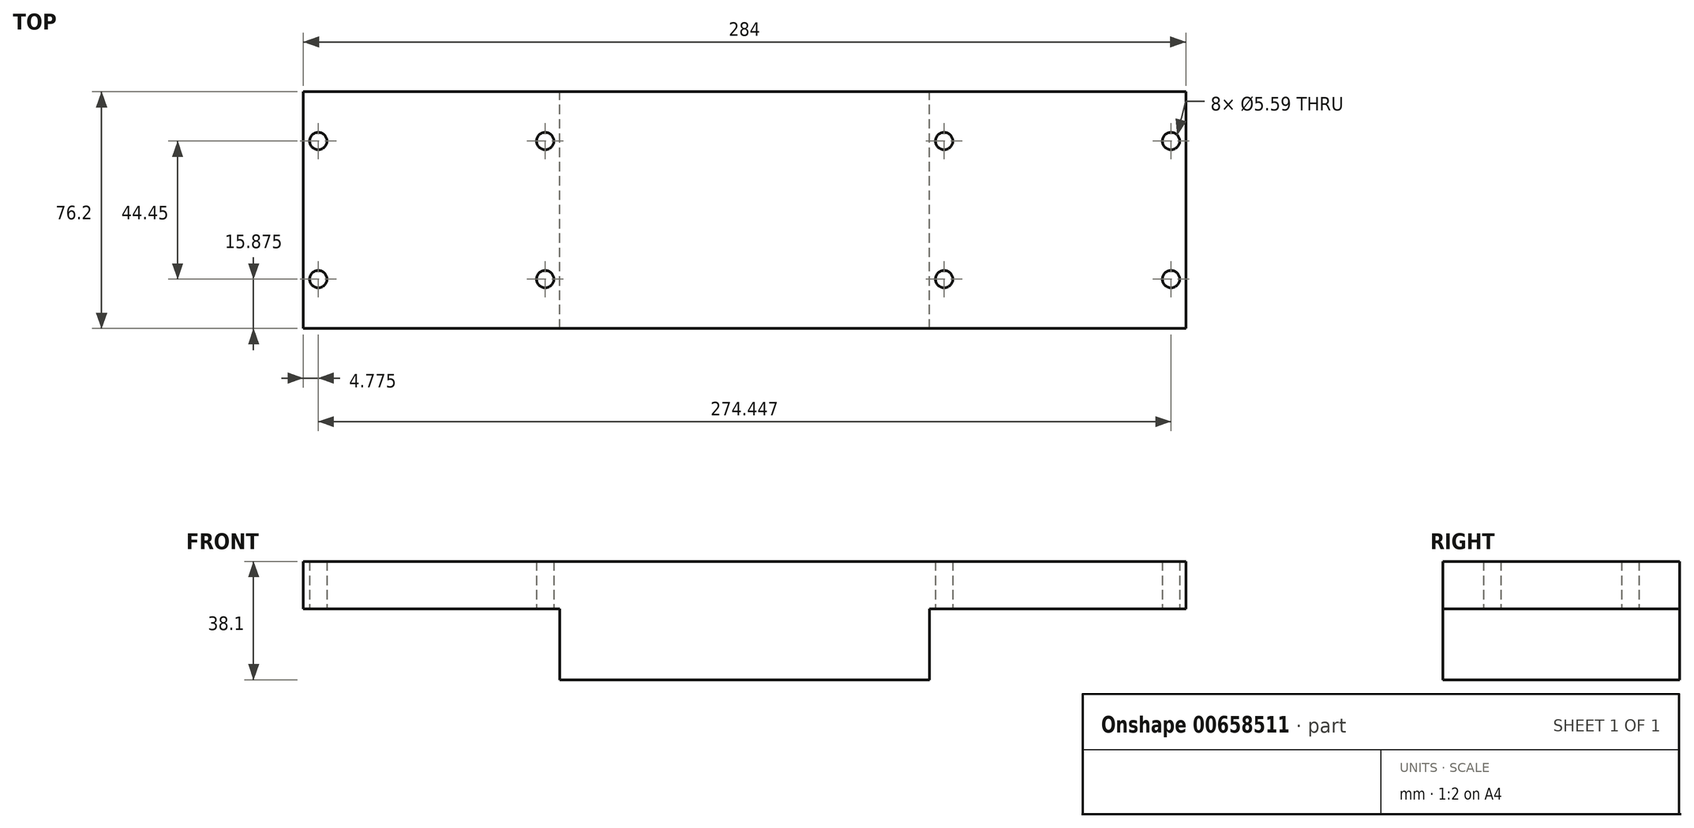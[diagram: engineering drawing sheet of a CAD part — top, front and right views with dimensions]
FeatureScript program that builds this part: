
annotation { "Feature Type Name" : "Feature", "Feature Type Description" : "" }
export const myFeature = defineFeature(function(context is Context, id is Id, definition is map)
    precondition{}
    {
        {
            var Q0;
            Q0=qCreatedBy(makeId("Top.planeOp"),FACE);
            var sketch = newSketch(context, id + "F0", { "sketchPlane" : qUnion([Q0])});
            skLineSegment(sketch, "E0.bottom", {"start": v(0, 0) * mm, "end": v(284, 0) * mm});
            skLineSegment(sketch, "E0.top", {"start": v(0, -76.2) * mm, "end": v(284, -76.2) * mm});
            skLineSegment(sketch, "E0.left", {"start": v(0, 0) * mm, "end": v(0, -76.2) * mm});
            skLineSegment(sketch, "E0.right", {"start": v(284, 0) * mm, "end": v(284, -76.2) * mm});
            skSolve(sketch);
        }
        {
            var Q0;
            Q0=makeQuery(id+"F0.imprint","IMPRINT",FACE,{"disambiguationData":[TD([[makeQuery(id+"F0.imprint","IMPRINT",EDGE,{"derivedFrom":sQuery(id+"F0.wireOp",EDGE,"E0.bottom")}),-1.0]])]});
            extrude(context, id + "F1", {"entities" : qUnion([Q0]), "oppositeDirection" : true, "depth" : 38.1 * mm, "offsetDistance" : 25.4 * mm});
        }
        {
            var Q0;
            Q0=makeQuery(id+"F1.opExtrude","CAP_FACE",FACE,{"disambiguationData":[OSD([sQuery(id+"F0.wireOp",EDGE,"E0.bottom"),sQuery(id+"F0.wireOp",EDGE,"E0.top"),sQuery(id+"F0.wireOp",EDGE,"E0.left"),sQuery(id+"F0.wireOp",EDGE,"E0.right")])],"isStart":false});
            var sketch = newSketch(context, id + "F2", { "sketchPlane" : qUnion([Q0])});
            skLineSegment(sketch, "E1.bottom", {"start": v(0, 76.2) * mm, "end": v(82.55, 76.2) * mm});
            skLineSegment(sketch, "E1.top", {"start": v(0, 0) * mm, "end": v(82.55, 0) * mm});
            skLineSegment(sketch, "E1.left", {"start": v(0, 76.2) * mm, "end": v(0, 0) * mm});
            skLineSegment(sketch, "E1.right", {"start": v(82.55, 76.2) * mm, "end": v(82.55, 0) * mm});
            skLineSegment(sketch, "E2.bottom", {"start": v(284, 76.2) * mm, "end": v(201.45, 76.2) * mm});
            skLineSegment(sketch, "E2.top", {"start": v(284, 0) * mm, "end": v(201.45, 0) * mm});
            skLineSegment(sketch, "E2.left", {"start": v(284, 76.2) * mm, "end": v(284, 0) * mm});
            skLineSegment(sketch, "E2.right", {"start": v(201.45, 76.2) * mm, "end": v(201.45, 0) * mm});
            skSolve(sketch);
        }
        {
            var Q0;
            Q0=makeQuery(id+"F2.imprint","IMPRINT",FACE,{"disambiguationData":[TD([[makeQuery(id+"F2.imprint","IMPRINT",EDGE,{"derivedFrom":sQuery(id+"F2.wireOp",EDGE,"E1.bottom")}),-1.0]])]});
            var sketch = newSketch(context, id + "F3", { "sketchPlane" : qUnion([Q0])});
            skCircle(sketch, "E3", {"center": v(4.78, 60.32) * mm, "radius": 2.8 * mm});
            skCircle(sketch, "E4.0.1.0", {"center": v(4.78, 15.87) * mm, "radius": 2.8 * mm});
            skCircle(sketch, "E4.1.0.0", {"center": v(77.8, 60.32) * mm, "radius": 2.8 * mm});
            skCircle(sketch, "E4.1.1.0", {"center": v(77.8, 15.87) * mm, "radius": 2.8 * mm});
            skLineSegment(sketch, "E4.direction1", {"start": v(4.78, 60.32) * mm, "end": v(77.8, 60.32) * mm, "construction": true});
            skLineSegment(sketch, "E4.direction2", {"start": v(4.78, 60.32) * mm, "end": v(4.78, 15.87) * mm, "construction": true});
            skSolve(sketch);
        }
        {
            var Q0;
            Q0=makeQuery(id+"F2.imprint","IMPRINT",FACE,{"disambiguationData":[TD([[makeQuery(id+"F2.imprint","IMPRINT",EDGE,{"derivedFrom":sQuery(id+"F2.wireOp",EDGE,"E2.bottom")}),-1.0]])]});
            var sketch = newSketch(context, id + "F4", { "sketchPlane" : qUnion([Q0])});
            skCircle(sketch, "E5", {"center": v(279.22, 60.32) * mm, "radius": 2.8 * mm});
            skCircle(sketch, "E6.0.1.0", {"center": v(279.22, 15.87) * mm, "radius": 2.8 * mm});
            skCircle(sketch, "E6.1.0.0", {"center": v(206.2, 60.32) * mm, "radius": 2.8 * mm});
            skCircle(sketch, "E6.1.1.0", {"center": v(206.2, 15.87) * mm, "radius": 2.8 * mm});
            skLineSegment(sketch, "E6.direction1", {"start": v(279.22, 60.32) * mm, "end": v(206.2, 60.32) * mm, "construction": true});
            skLineSegment(sketch, "E6.direction2", {"start": v(279.22, 60.32) * mm, "end": v(279.22, 15.87) * mm, "construction": true});
            skSolve(sketch);
        }
        {
            var Q0;
            Q0=makeQuery(id+"F4.imprint","IMPRINT",FACE,{"disambiguationData":[TD([[makeQuery(id+"F4.imprint","IMPRINT",EDGE,{"derivedFrom":sQuery(id+"F4.wireOp",EDGE,"E6.0.1.0")}),1.0]])]});
            var Q1;
            Q1=makeQuery(id+"F4.imprint","IMPRINT",FACE,{"disambiguationData":[TD([[makeQuery(id+"F4.imprint","IMPRINT",EDGE,{"derivedFrom":sQuery(id+"F4.wireOp",EDGE,"E5")}),1.0]])]});
            var Q2;
            Q2=makeQuery(id+"F4.imprint","IMPRINT",FACE,{"disambiguationData":[TD([[makeQuery(id+"F4.imprint","IMPRINT",EDGE,{"derivedFrom":sQuery(id+"F4.wireOp",EDGE,"E6.1.0.0")}),1.0]])]});
            var Q3;
            Q3=makeQuery(id+"F4.imprint","IMPRINT",FACE,{"disambiguationData":[TD([[makeQuery(id+"F4.imprint","IMPRINT",EDGE,{"derivedFrom":sQuery(id+"F4.wireOp",EDGE,"E6.1.1.0")}),1.0]])]});
            var Q4;
            Q4=makeQuery(id+"F3.imprint","IMPRINT",FACE,{"disambiguationData":[TD([[makeQuery(id+"F3.imprint","IMPRINT",EDGE,{"derivedFrom":sQuery(id+"F3.wireOp",EDGE,"E4.1.0.0")}),1.0]])]});
            var Q5;
            Q5=makeQuery(id+"F3.imprint","IMPRINT",FACE,{"disambiguationData":[TD([[makeQuery(id+"F3.imprint","IMPRINT",EDGE,{"derivedFrom":sQuery(id+"F3.wireOp",EDGE,"E4.1.1.0")}),1.0]])]});
            var Q6;
            Q6=makeQuery(id+"F3.imprint","IMPRINT",FACE,{"disambiguationData":[TD([[makeQuery(id+"F3.imprint","IMPRINT",EDGE,{"derivedFrom":sQuery(id+"F3.wireOp",EDGE,"E4.0.1.0")}),1.0]])]});
            var Q7;
            Q7=makeQuery(id+"F3.imprint","IMPRINT",FACE,{"disambiguationData":[TD([[makeQuery(id+"F3.imprint","IMPRINT",EDGE,{"derivedFrom":sQuery(id+"F3.wireOp",EDGE,"E3")}),1.0]])]});
            extrude(context, id + "F5", {"entities" : qUnion([Q0, Q1, Q2, Q3, Q4, Q5, Q6, Q7]), "operationType" : NewBodyOperationType.REMOVE, "endBound" : BoundingType.THROUGH_ALL, "oppositeDirection" : true, "depth" : 25.4 * mm, "offsetDistance" : 25.4 * mm});
        }
        {
            var Q0;
            Q0=makeQuery(id+"F2.imprint","IMPRINT",FACE,{"disambiguationData":[TD([[makeQuery(id+"F2.imprint","IMPRINT",EDGE,{"derivedFrom":sQuery(id+"F2.wireOp",EDGE,"E1.bottom")}),-1.0]])]});
            var Q1;
            Q1=makeQuery(id+"F2.imprint","IMPRINT",FACE,{"disambiguationData":[TD([[makeQuery(id+"F2.imprint","IMPRINT",EDGE,{"derivedFrom":sQuery(id+"F2.wireOp",EDGE,"E2.bottom")}),-1.0]])]});
            extrude(context, id + "F6", {"entities" : qUnion([Q0, Q1]), "operationType" : NewBodyOperationType.REMOVE, "oppositeDirection" : true, "depth" : 22.86 * mm, "offsetDistance" : 25.4 * mm});
        }
    });
